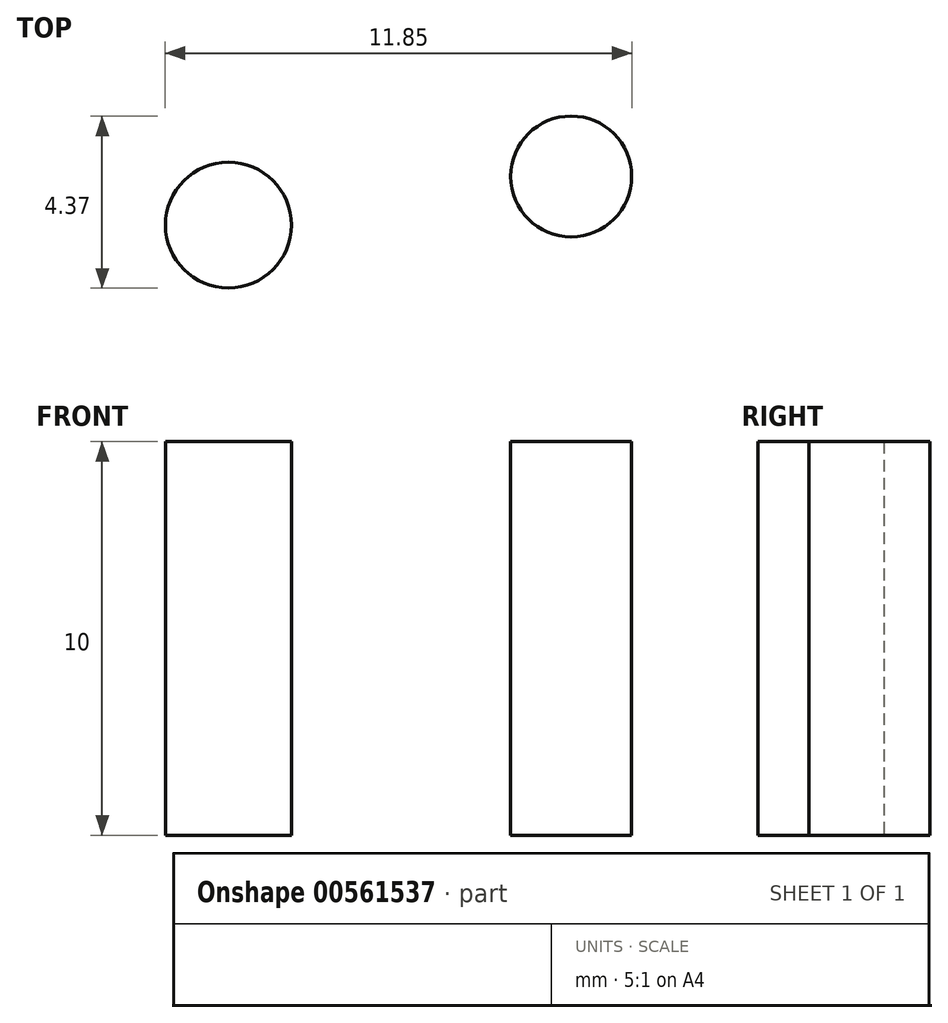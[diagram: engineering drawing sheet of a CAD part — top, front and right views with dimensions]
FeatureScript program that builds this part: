
annotation { "Feature Type Name" : "Feature", "Feature Type Description" : "" }
export const myFeature = defineFeature(function(context is Context, id is Id, definition is map)
    precondition{}
    {
        {
            var Q0;
            Q0=qCreatedBy(makeId("Top.planeOp"),FACE);
            var sketch = newSketch(context, id + "F0", { "sketchPlane" : qUnion([Q0])});
            skCircle(sketch, "E0", {"center": v(-5.78, 15.3) * mm, "radius": 1.6 * mm});
            skCircle(sketch, "E1", {"center": v(2.93, 16.54) * mm, "radius": 1.54 * mm});
            skSolve(sketch);
        }
        {
            var Q0;
            Q0=qSketchRegion(id+"F0",true);
            extrude(context, id + "F1", {"entities" : qUnion([Q0]), "depth" : 10 * mm, "offsetDistance" : 25 * mm});
        }
    });
